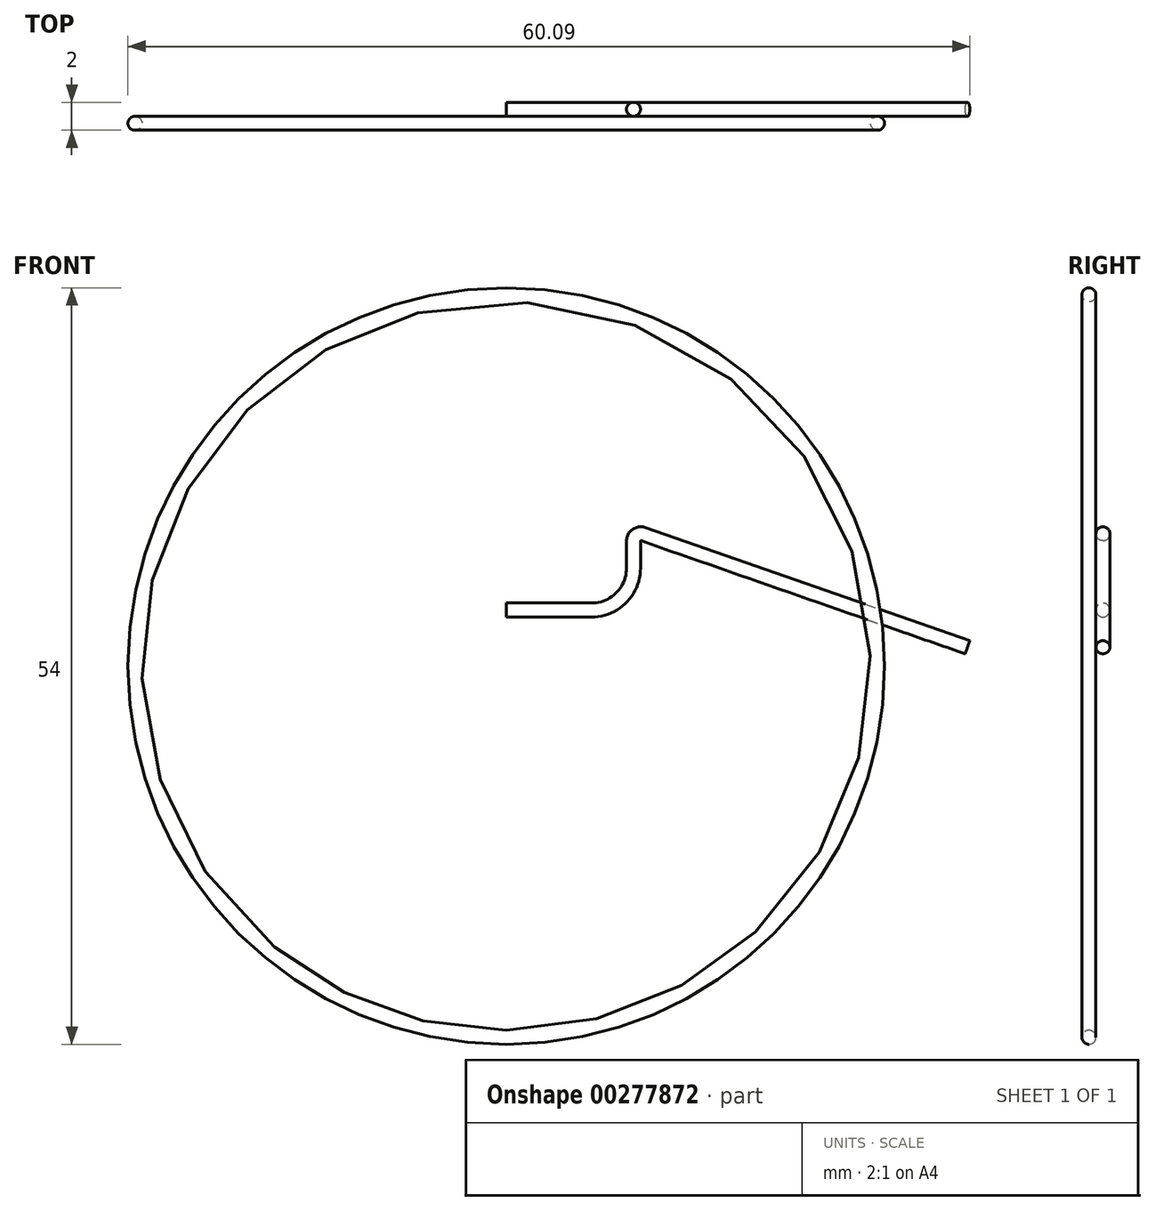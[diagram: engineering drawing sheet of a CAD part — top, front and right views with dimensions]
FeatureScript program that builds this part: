
annotation { "Feature Type Name" : "Feature", "Feature Type Description" : "" }
export const myFeature = defineFeature(function(context is Context, id is Id, definition is map)
    precondition{}
    {
        {
            var Q0;
            Q0=qCreatedBy(makeId("Front.planeOp"),FACE);
            var sketch = newSketch(context, id + "F0", { "sketchPlane" : qUnion([Q0])});
            skCircle(sketch, "E0", {"center": v(0, 0) * mm, "radius": 26.5 * mm});
            skSolve(sketch);
        }
        {
            var Q0;
            Q0=qCreatedBy(makeId("Right.planeOp"),FACE);
            var sketch = newSketch(context, id + "F1", { "sketchPlane" : qUnion([Q0])});
            skLineSegment(sketch, "E1.0", {"start": v(0, -26.5) * mm, "end": v(0, 26.5) * mm});
            skCircle(sketch, "E2", {"center": v(0, 26.5) * mm, "radius": 0.5 * mm});
            skSolve(sketch);
        }
        {
            var Q0;
            Q0 = qSketchRegion(id + "F1", true);
            var Q1;
            Q1 = qConstructionFilter(qBodyType(qCreatedBy(id + "F0" ,EDGE), BodyType.WIRE), ConstructionObject.NO);
            sweep(context, id + "F2", {"profiles" : qUnion([Q0]), "path" : qUnion([Q1])});
        }
        {
            var Q0;
            Q0=qCreatedBy(makeId("Front.planeOp"),FACE);
            var sketch = newSketch(context, id + "F3", { "sketchPlane" : qUnion([Q0])});
            skCircle(sketch, "E3", {"center": v(0, 0) * mm, "radius": 19 * mm});
            skCircle(sketch, "E4", {"center": v(0, 0) * mm, "radius": 26 * mm, "construction": true});
            skSolve(sketch);
        }
        {
            var Q0;
            Q0=qCreatedBy(makeId("Top.planeOp"),FACE);
            var sketch = newSketch(context, id + "F4", { "sketchPlane" : qUnion([Q0])});
            skLineSegment(sketch, "E5.0", {"start": v(19, 0) * mm, "end": v(-19, 0) * mm, "construction": true});
            skCircle(sketch, "E6", {"center": v(-19, 0) * mm, "radius": 0.5 * mm});
            skSolve(sketch);
        }
        {
            var Q0;
            Q0=qCreatedBy(makeId("Right.planeOp"),FACE);
            var sketch = newSketch(context, id + "F5", { "sketchPlane" : qUnion([Q0])});
            skLineSegment(sketch, "E7", {"start": v(-0.5, -26.5) * mm, "end": v(-0.5, 26.5) * mm, "construction": true});
            skArc(sketch, "E8", {"start": v(-0.5, 26.5) * mm, "mid": v(0, 26) * mm, "end": v(0.5, 26.5) * mm, "construction": true});
            skLineSegment(sketch, "E9", {"start": v(0.5, -26.5) * mm, "end": v(0.5, 26.5) * mm, "construction": true});
            skCircle(sketch, "E10", {"center": v(1, 4) * mm, "radius": 0.5 * mm});
            skSolve(sketch);
        }
        {
            var Q0;
            Q0=qCreatedBy(makeId("Front.planeOp"),FACE);
            cPlane(context, id + "F6", {"entities" : qUnion([Q0]), "cplaneType" : CPlaneType.OFFSET, "offset" : 1 * mm, "oppositeDirection" : true, "width" : 150 * mm, "height" : 150 * mm});
        }
        {
            var Q0;
            Q0=qCreatedBy(id+"F6.planeOp",FACE);
            var sketch = newSketch(context, id + "F7", { "sketchPlane" : qUnion([Q0])});
            skPoint(sketch, "E11.0", {"position": v(0, 4) * mm});
            skLineSegment(sketch, "E12", {"start": v(0, 4) * mm, "end": v(6.09, 4) * mm});
            skLineSegment(sketch, "E13", {"start": v(9.09, 7) * mm, "end": v(9.09, 8.93) * mm});
            skLineSegment(sketch, "E14", {"start": v(9.78, 9.42) * mm, "end": v(32.93, 1.35) * mm});
            skPoint(sketch, "E15.visualSharp", {"position": v(9.09, 4) * mm});
            skArc(sketch, "E15.filletArc", {"start": v(6.09, 4) * mm, "mid": v(8.2, 4.88) * mm, "end": v(9.09, 7) * mm});
            skPoint(sketch, "E16.visualSharp", {"position": v(9.09, 9.66) * mm});
            skArc(sketch, "E16.filletArc", {"start": v(9.78, 9.42) * mm, "mid": v(9.3, 9.35) * mm, "end": v(9.09, 8.93) * mm});
            skSolve(sketch);
        }
        {
            var Q0;
            Q0 = qSketchRegion(id + "F5", true);
            var Q1;
            Q1 = qConstructionFilter(qBodyType(qCreatedBy(id + "F7" ,EDGE), BodyType.WIRE), ConstructionObject.NO);
            sweep(context, id + "F8", {"profiles" : qUnion([Q0]), "path" : qUnion([Q1])});
        }
    });
